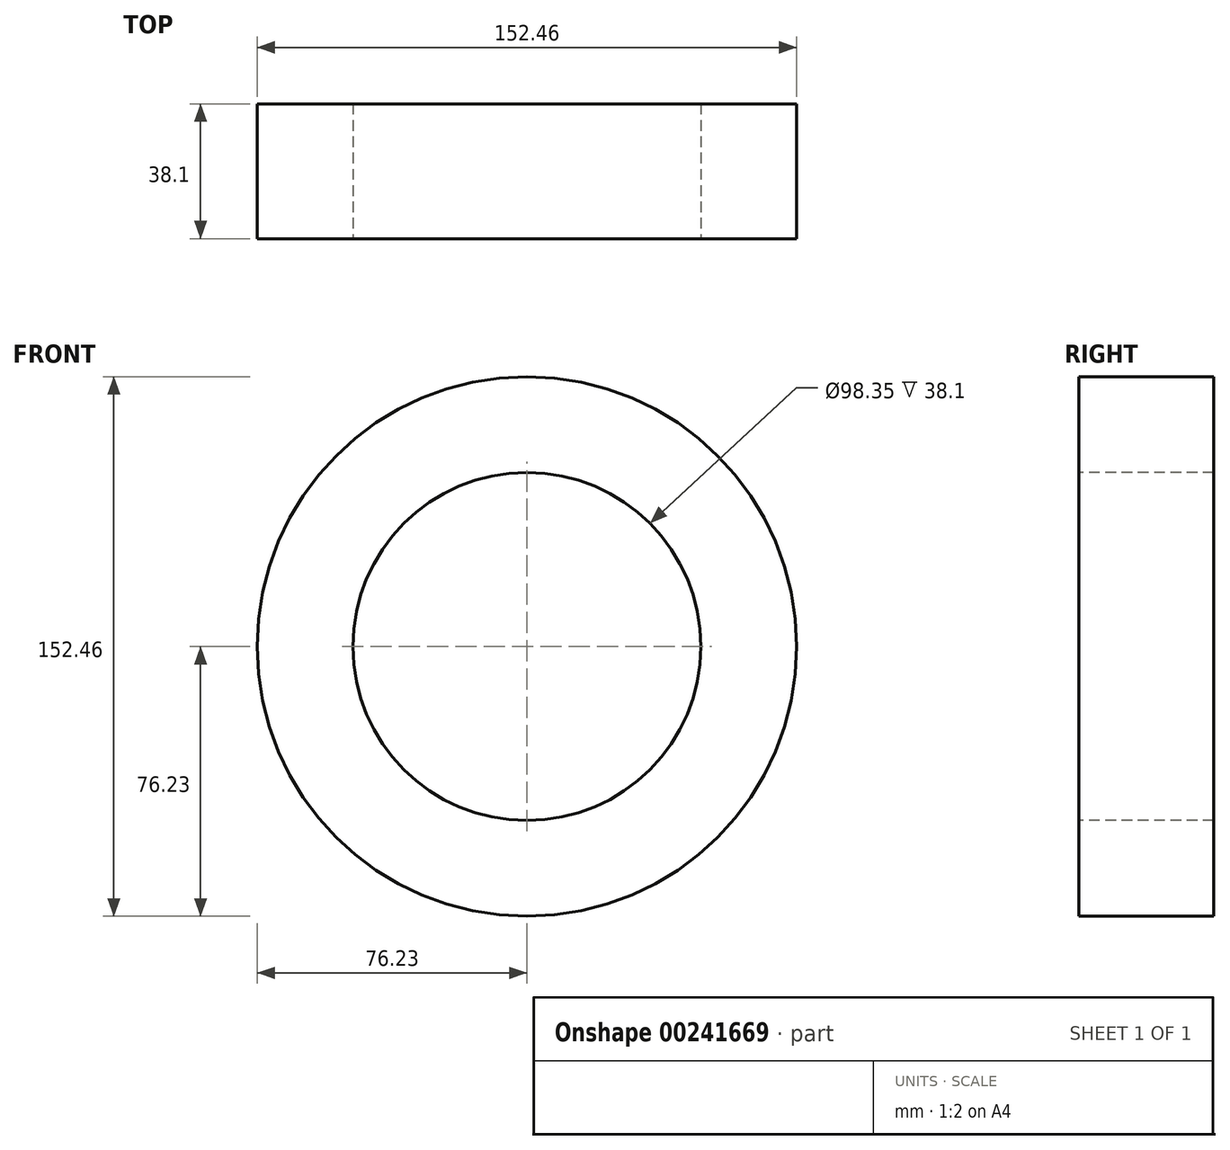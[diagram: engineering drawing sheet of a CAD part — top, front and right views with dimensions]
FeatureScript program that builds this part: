
annotation { "Feature Type Name" : "Feature", "Feature Type Description" : "" }
export const myFeature = defineFeature(function(context is Context, id is Id, definition is map)
    precondition{}
    {
        {
            var Q0;
            Q0=qCreatedBy(makeId("Front.planeOp"),FACE);
            var sketch = newSketch(context, id + "F0", { "sketchPlane" : qUnion([Q0])});
            skCircle(sketch, "E0", {"center": v(0, 0) * mm, "radius": 76.23 * mm});
            skCircle(sketch, "E1", {"center": v(0, 0) * mm, "radius": 49.17 * mm});
            skSolve(sketch);
        }
        {
            var Q0;
            Q0=makeQuery(id+"F0.imprint","IMPRINT",FACE,{"disambiguationData":[TD([[makeQuery(id+"F0.imprint","IMPRINT",EDGE,{"derivedFrom":sQuery(id+"F0.wireOp",EDGE,"E0")}),1.0]])]});
            var Q1;
            Q1=makeQuery(id+"F0.imprint","IMPRINT",FACE,{"disambiguationData":[TD([[makeQuery(id+"F0.imprint","IMPRINT",EDGE,{"derivedFrom":sQuery(id+"F0.wireOp",EDGE,"E1")}),-1.0]])]});
            extrude(context, id + "F1", {"entities" : qUnion([Q0, Q1]), "endBound" : BoundingType.SYMMETRIC, "oppositeDirection" : true, "depth" : 38.1 * mm});
        }
    });
